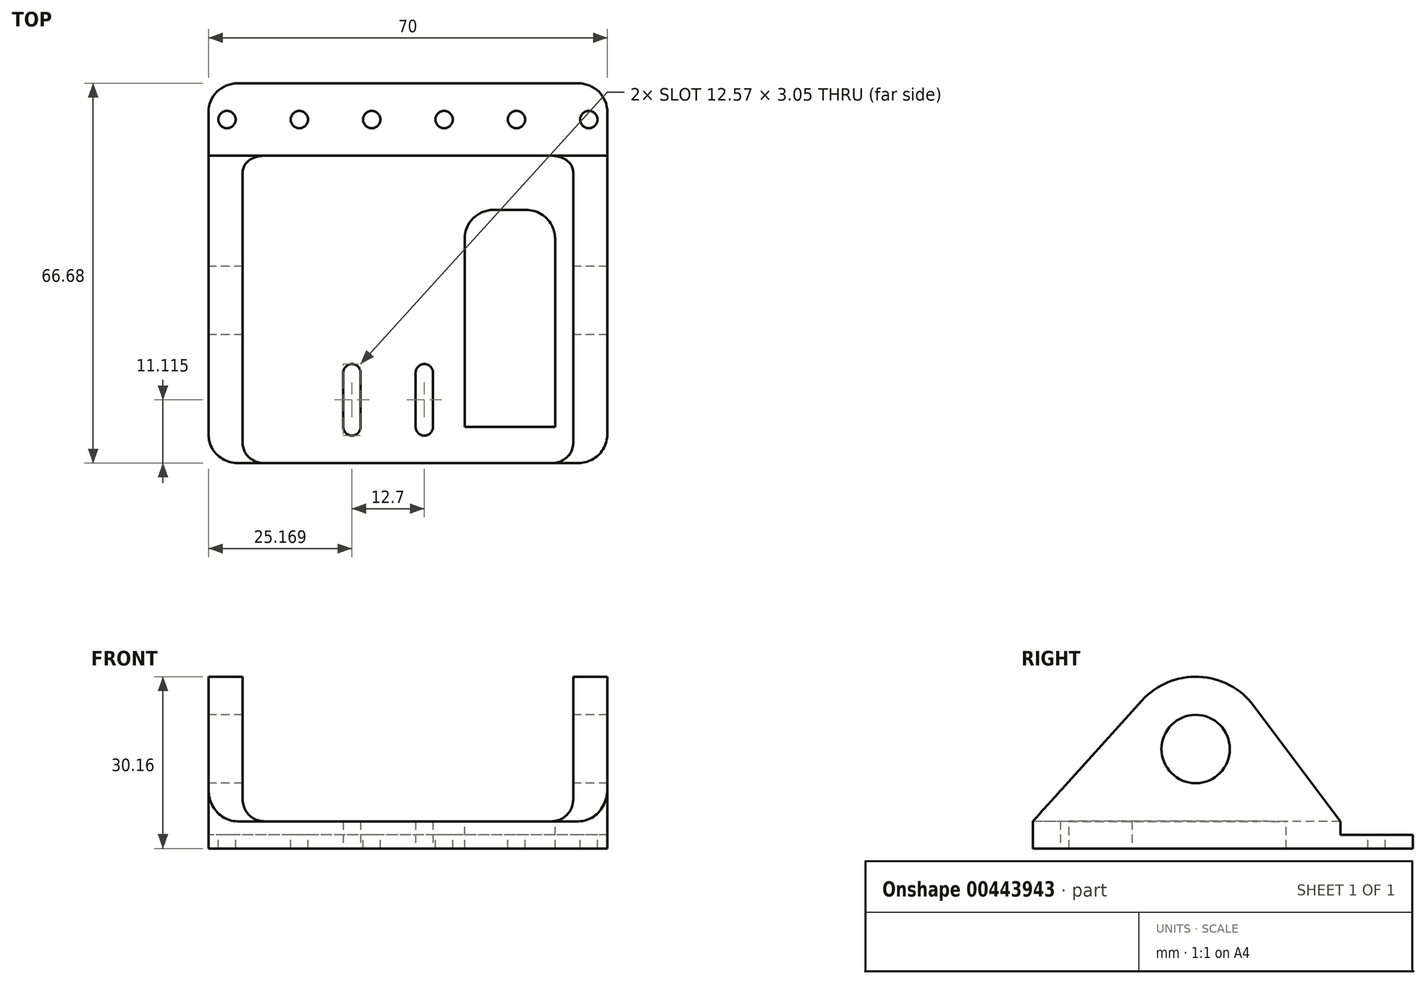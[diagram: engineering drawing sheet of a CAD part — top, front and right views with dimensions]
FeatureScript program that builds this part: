
annotation { "Feature Type Name" : "Feature", "Feature Type Description" : "" }
export const myFeature = defineFeature(function(context is Context, id is Id, definition is map)
    precondition{}
    {
        {
            var Q0;
            Q0=qCreatedBy(makeId("Top.planeOp"),FACE);
            var sketch = newSketch(context, id + "F0", { "sketchPlane" : qUnion([Q0])});
            skLineSegment(sketch, "E0.bottom", {"start": v(35, 33.34) * mm, "end": v(-35, 33.34) * mm});
            skLineSegment(sketch, "E0.top", {"start": v(35, -33.34) * mm, "end": v(-35, -33.34) * mm});
            skLineSegment(sketch, "E0.left", {"start": v(35, 33.34) * mm, "end": v(35, -33.34) * mm});
            skLineSegment(sketch, "E0.right", {"start": v(-35, 33.34) * mm, "end": v(-35, -33.34) * mm});
            skPoint(sketch, "E0.middle", {"position": v(0, 0) * mm});
            skSolve(sketch);
        }
        {
            var Q0;
            Q0=qSketchRegion(id+"F0",true);
            extrude(context, id + "F1", {"entities" : qUnion([Q0]), "depth" : 4.76 * mm});
        }
        {
            var Q0;
            Q0=makeQuery(id+"F1.opExtrude","SWEPT_FACE",FACE,{"disambiguationData":[OSD([sQuery(id+"F0.wireOp",EDGE,"E0.right")])]});
            var sketch = newSketch(context, id + "F2", { "sketchPlane" : qUnion([Q0])});
            skCircle(sketch, "E1", {"center": v(4.76, 17.46) * mm, "radius": 2 * mm});
            skCircle(sketch, "E2", {"center": v(4.76, 17.46) * mm, "radius": 6 * mm});
            skLineSegment(sketch, "E3", {"start": v(-7.94, 17.46) * mm, "end": v(-7.94, 4.76) * mm});
            skLineSegment(sketch, "E4", {"start": v(-7.94, 4.76) * mm, "end": v(17.46, 4.76) * mm});
            skLineSegment(sketch, "E5", {"start": v(17.46, 4.76) * mm, "end": v(17.46, 17.46) * mm});
            skArc(sketch, "E6", {"start": v(-7.94, 17.46) * mm, "mid": v(-4.22, 8.48) * mm, "end": v(4.76, 4.76) * mm, "construction": true});
            skArc(sketch, "E7", {"start": v(4.76, 4.76) * mm, "mid": v(13.74, 8.48) * mm, "end": v(17.46, 17.46) * mm, "construction": true});
            skArc(sketch, "E8", {"start": v(17.46, 17.46) * mm, "mid": v(4.76, 30.16) * mm, "end": v(-7.94, 17.46) * mm});
            skLineSegment(sketch, "E9", {"start": v(14.19, 25.97) * mm, "end": v(33.34, 4.76) * mm});
            skLineSegment(sketch, "E10", {"start": v(33.34, 4.76) * mm, "end": v(17.46, 4.76) * mm});
            skLineSegment(sketch, "E11", {"start": v(-5.4, 25.08) * mm, "end": v(-20.64, 4.76) * mm});
            skLineSegment(sketch, "E12", {"start": v(-20.64, 4.76) * mm, "end": v(-7.94, 4.76) * mm});
            skSolve(sketch);
        }
        {
            var Q0;
            Q0=qSketchRegion(id+"F2",true);
            var Q1;
            Q1=makeQuery(id+"F1.opExtrude","SWEPT_FACE",FACE,{"disambiguationData":[OSD([sQuery(id+"F0.wireOp",EDGE,"E0.left")])]});
            extrude(context, id + "F3", {"entities" : qUnion([Q0]), "operationType" : NewBodyOperationType.ADD, "endBound" : BoundingType.UP_TO_SURFACE, "oppositeDirection" : true, "endBoundEntityFace" : qUnion([Q1]), "depth" : 25.4 * mm});
        }
        {
            var Q0;
            Q0=makeQuery(id+"F1.opExtrude","CAP_FACE",FACE,{"disambiguationData":[OSD([sQuery(id+"F0.wireOp",EDGE,"E0.bottom"),sQuery(id+"F0.wireOp",EDGE,"E0.top"),sQuery(id+"F0.wireOp",EDGE,"E0.left"),sQuery(id+"F0.wireOp",EDGE,"E0.right")])],"isStart":false});
            var sketch = newSketch(context, id + "F4", { "sketchPlane" : qUnion([Q0])});
            skLineSegment(sketch, "E13.bottom", {"start": v(-29, 20.64) * mm, "end": v(29, 20.64) * mm});
            skLineSegment(sketch, "E13.top", {"start": v(-29, -33.34) * mm, "end": v(29, -33.34) * mm});
            skLineSegment(sketch, "E13.left", {"start": v(-29, 20.64) * mm, "end": v(-29, -33.34) * mm});
            skLineSegment(sketch, "E13.right", {"start": v(29, 20.64) * mm, "end": v(29, -33.34) * mm});
            skSolve(sketch);
        }
        {
            var Q0;
            Q0=qSketchRegion(id+"F4",true);
            extrude(context, id + "F5", {"entities" : qUnion([Q0]), "operationType" : NewBodyOperationType.REMOVE, "endBound" : BoundingType.THROUGH_ALL, "depth" : 25.4 * mm});
        }
        {
            var Q0;
            Q0=makeQuery(id+"F5.boolean.opBoolean","MERGE",FACE,{"derivedFrom":[makeQuery(id+"F1.opExtrude","CAP_FACE",FACE,{"disambiguationData":[OSD([sQuery(id+"F0.wireOp",EDGE,"E0.bottom"),sQuery(id+"F0.wireOp",EDGE,"E0.top"),sQuery(id+"F0.wireOp",EDGE,"E0.left"),sQuery(id+"F0.wireOp",EDGE,"E0.right")])],"isStart":false}),makeQuery(id+"F5.opExtrude","CAP_FACE",FACE,{"disambiguationData":[OSD([sQuery(id+"F4.wireOp",EDGE,"E13.bottom"),sQuery(id+"F4.wireOp",EDGE,"E13.top"),sQuery(id+"F4.wireOp",EDGE,"E13.left"),sQuery(id+"F4.wireOp",EDGE,"E13.right")])],"isStart":true})]});
            var sketch = newSketch(context, id + "F6", { "sketchPlane" : qUnion([Q0])});
            skLineSegment(sketch, "E14.bottom", {"start": v(25.83, -26.99) * mm, "end": v(9.95, -26.99) * mm});
            skLineSegment(sketch, "E14.top", {"start": v(25.83, 11.11) * mm, "end": v(9.95, 11.11) * mm});
            skLineSegment(sketch, "E14.left", {"start": v(25.83, -26.99) * mm, "end": v(25.83, 11.11) * mm});
            skLineSegment(sketch, "E14.right", {"start": v(9.95, -26.99) * mm, "end": v(9.95, 11.11) * mm});
            skSolve(sketch);
        }
        {
            var Q0;
            Q0=qSketchRegion(id+"F6",true);
            extrude(context, id + "F7", {"entities" : qUnion([Q0]), "operationType" : NewBodyOperationType.REMOVE, "endBound" : BoundingType.UP_TO_NEXT, "oppositeDirection" : true, "depth" : 25.4 * mm});
        }
        {
            var Q0;
            Q0=makeQuery(id+"F1.opExtrude","CAP_FACE",FACE,{"disambiguationData":[OSD([sQuery(id+"F0.wireOp",EDGE,"E0.bottom"),sQuery(id+"F0.wireOp",EDGE,"E0.top"),sQuery(id+"F0.wireOp",EDGE,"E0.left"),sQuery(id+"F0.wireOp",EDGE,"E0.right")])],"isStart":true});
            var sketch = newSketch(context, id + "F8", { "sketchPlane" : qUnion([Q0])});
            skLineSegment(sketch, "E15.bottom", {"start": v(-15.8, 33.34) * mm, "end": v(8.84, 33.34) * mm, "construction": true});
            skLineSegment(sketch, "E15.top", {"start": v(-15.8, 4.35) * mm, "end": v(8.84, 4.35) * mm, "construction": true});
            skLineSegment(sketch, "E15.left", {"start": v(-15.8, 33.34) * mm, "end": v(-15.8, 4.35) * mm, "construction": true});
            skLineSegment(sketch, "E15.right", {"start": v(8.84, 33.34) * mm, "end": v(8.84, 4.35) * mm, "construction": true});
            skLineSegment(sketch, "E16", {"start": v(-15.8, 22.23) * mm, "end": v(-9.83, 22.23) * mm, "construction": true});
            skLineSegment(sketch, "E17", {"start": v(2.87, 22.23) * mm, "end": v(8.84, 22.23) * mm, "construction": true});
            skLineSegment(sketch, "E18", {"start": v(-9.83, 22.23) * mm, "end": v(2.87, 22.23) * mm, "construction": true});
            skLineSegment(sketch, "E19.bottom", {"start": v(-11.35, 17.46) * mm, "end": v(-8.3, 17.46) * mm, "construction": true});
            skLineSegment(sketch, "E19.top", {"start": v(-11.35, 26.99) * mm, "end": v(-8.3, 26.99) * mm, "construction": true});
            skLineSegment(sketch, "E19.left", {"start": v(-11.35, 17.46) * mm, "end": v(-11.35, 26.99) * mm});
            skLineSegment(sketch, "E19.right", {"start": v(-8.3, 17.46) * mm, "end": v(-8.3, 26.99) * mm});
            skPoint(sketch, "E19.middle", {"position": v(-9.83, 22.23) * mm});
            skLineSegment(sketch, "E20.bottom", {"start": v(1.34, 17.46) * mm, "end": v(4.4, 17.46) * mm, "construction": true});
            skLineSegment(sketch, "E20.top", {"start": v(1.35, 26.99) * mm, "end": v(4.4, 26.99) * mm, "construction": true});
            skLineSegment(sketch, "E20.left", {"start": v(1.35, 17.46) * mm, "end": v(1.35, 26.99) * mm});
            skLineSegment(sketch, "E20.right", {"start": v(4.4, 17.46) * mm, "end": v(4.4, 26.99) * mm});
            skPoint(sketch, "E20.middle", {"position": v(2.87, 22.23) * mm});
            skArc(sketch, "E21", {"start": v(-11.35, 17.46) * mm, "mid": v(-9.83, 15.94) * mm, "end": v(-8.3, 17.46) * mm});
            skArc(sketch, "E22", {"start": v(1.34, 17.46) * mm, "mid": v(2.87, 15.94) * mm, "end": v(4.4, 17.46) * mm});
            skArc(sketch, "E23", {"start": v(-8.3, 26.99) * mm, "mid": v(-9.83, 28.51) * mm, "end": v(-11.35, 26.99) * mm});
            skArc(sketch, "E24", {"start": v(4.4, 26.99) * mm, "mid": v(2.87, 28.51) * mm, "end": v(1.35, 26.99) * mm});
            skSolve(sketch);
        }
        {
            var Q0;
            Q0=makeQuery(id+"F8.imprint","IMPRINT",FACE,{"disambiguationData":[TD([[makeQuery(id+"F8.imprint","IMPRINT",EDGE,{"derivedFrom":sQuery(id+"F8.wireOp",EDGE,"E20.left")}),-1.0]])]});
            var Q1;
            Q1=makeQuery(id+"F8.imprint","IMPRINT",FACE,{"disambiguationData":[TD([[makeQuery(id+"F8.imprint","IMPRINT",EDGE,{"derivedFrom":sQuery(id+"F8.wireOp",EDGE,"E19.left")}),-1.0]])]});
            extrude(context, id + "F9", {"entities" : qUnion([Q0, Q1]), "operationType" : NewBodyOperationType.REMOVE, "oppositeDirection" : true, "depth" : 25.4 * mm});
        }
        {
            var Q0;
            Q0=makeQuery(id+"FCm2X9aqr08QVEI_1.splitOp","SPLIT",FACE,{"derivedFrom":makeQuery(id+"FB7dtnONbZpMkYq_1.boolean.opBoolean","MERGE",FACE,{"derivedFrom":[makeQuery(id+"FMi2k5xwuVLF3PA_1.boolean.opBoolean","MERGE",FACE,{"derivedFrom":[makeQuery(id+"F5.boolean.opBoolean","MERGE",FACE,{"derivedFrom":[makeQuery(id+"F1.opExtrude","CAP_FACE",FACE,{"disambiguationData":[OSD([sQuery(id+"F0.wireOp",EDGE,"E0.bottom"),sQuery(id+"F0.wireOp",EDGE,"E0.top"),sQuery(id+"F0.wireOp",EDGE,"E0.left"),sQuery(id+"F0.wireOp",EDGE,"E0.right")])],"isStart":false}),makeQuery(id+"F5.opExtrude","CAP_FACE",FACE,{"disambiguationData":[OSD([sQuery(id+"F4.wireOp",EDGE,"E13.bottom"),sQuery(id+"F4.wireOp",EDGE,"E13.top"),sQuery(id+"F4.wireOp",EDGE,"E13.left"),sQuery(id+"F4.wireOp",EDGE,"E13.right")])],"isStart":true})]}),makeQuery(id+"FMi2k5xwuVLF3PA_1.opExtrude","CAP_FACE",FACE,{"disambiguationData":[OSD([sQuery(id+"FTfkWxI29d7fm9c_1.wireOp",EDGE,"U5VrA20J-yWmg-0HZa-dIx8-nOMwWomhaKgW.bottom"),sQuery(id+"FTfkWxI29d7fm9c_1.wireOp",EDGE,"U5VrA20J-yWmg-0HZa-dIx8-nOMwWomhaKgW.top"),sQuery(id+"FTfkWxI29d7fm9c_1.wireOp",EDGE,"U5VrA20J-yWmg-0HZa-dIx8-nOMwWomhaKgW.left"),sQuery(id+"FTfkWxI29d7fm9c_1.wireOp",EDGE,"U5VrA20J-yWmg-0HZa-dIx8-nOMwWomhaKgW.right")])],"isStart":false})]}),makeQuery(id+"FB7dtnONbZpMkYq_1.opExtrude","CAP_FACE",FACE,{"disambiguationData":[OSD([sQuery(id+"FrBCCQyiW6SgCSX_1.wireOp",EDGE,"mjBH3HNc-4qiW-W3lP-ZLe8-cYrq6YZMYFNo"),sQuery(id+"FrBCCQyiW6SgCSX_1.wireOp",EDGE,"n0JCGPxu-1fb2-x5wm-e2xR-ESQF5aKrQkje"),sQuery(id+"FrBCCQyiW6SgCSX_1.wireOp",EDGE,"84PFO3UT-d6lO-mKTi-YjnM-evNH14zkO4eM"),sQuery(id+"FrBCCQyiW6SgCSX_1.wireOp",EDGE,"4GRO5FYG-KxOb-3d1O-tR9n-mdH5JcoPf6cH"),sQuery(id+"FrBCCQyiW6SgCSX_1.wireOp",EDGE,"m2es6RPa-RLP1-cTb9-RGGa-vc4GqjSnDQWD"),sQuery(id+"FrBCCQyiW6SgCSX_1.wireOp",EDGE,"UMJGmRyr-7NXd-P1yE-yibc-kyMIe0C5EN52"),sQuery(id+"FrBCCQyiW6SgCSX_1.wireOp",EDGE,"6lN2ZSX2-TrvR-bXuT-GwBE-q0yeGYqzIHT5")])],"isStart":false})]}),"isFromBackBody":true});
            var sketch = newSketch(context, id + "F10", { "sketchPlane" : qUnion([Q0])});
            skLineSegment(sketch, "E25.bottom", {"start": v(-35, 33.34) * mm, "end": v(35, 33.34) * mm});
            skLineSegment(sketch, "E25.top", {"start": v(-35, 20.64) * mm, "end": v(35, 20.64) * mm});
            skLineSegment(sketch, "E26", {"start": v(35, 20.64) * mm, "end": v(35, 33.34) * mm});
            skLineSegment(sketch, "E27", {"start": v(-35, 20.64) * mm, "end": v(-35, 33.34) * mm});
            skSolve(sketch);
        }
        {
            var Q0;
            Q0=qSketchRegion(id+"F10",true);
            extrude(context, id + "F11", {"entities" : qUnion([Q0]), "operationType" : NewBodyOperationType.REMOVE, "oppositeDirection" : true, "depth" : 2.38 * mm});
        }
        {
            var Q0;
            Q0=makeQuery(id+"F11.boolean.opBoolean","COPY",FACE,{"derivedFrom":makeQuery(id+"F11.opExtrude","CAP_FACE",FACE,{"disambiguationData":[OSD([sQuery(id+"F10.wireOp",EDGE,"E25.bottom"),sQuery(id+"F10.wireOp",EDGE,"E25.top"),sQuery(id+"F10.wireOp",EDGE,"E25.left"),sQuery(id+"F10.wireOp",EDGE,"E25.right")])],"isStart":false})});
            var sketch = newSketch(context, id + "F12", { "sketchPlane" : qUnion([Q0])});
            skLineSegment(sketch, "E28", {"start": v(-19.05, 26.99) * mm, "end": v(-6.35, 26.99) * mm, "construction": true});
            skLineSegment(sketch, "E29", {"start": v(-6.35, 26.99) * mm, "end": v(6.35, 26.99) * mm, "construction": true});
            skLineSegment(sketch, "E30", {"start": v(6.35, 26.99) * mm, "end": v(19.05, 26.99) * mm, "construction": true});
            skLineSegment(sketch, "E31", {"start": v(-19.05, 26.99) * mm, "end": v(-31.75, 26.99) * mm, "construction": true});
            skLineSegment(sketch, "E32", {"start": v(19.05, 26.99) * mm, "end": v(31.75, 26.99) * mm, "construction": true});
            skLineSegment(sketch, "E33", {"start": v(31.75, 26.99) * mm, "end": v(35, 26.99) * mm, "construction": true});
            skLineSegment(sketch, "E34", {"start": v(-31.75, 26.99) * mm, "end": v(-35, 26.99) * mm, "construction": true});
            skCircle(sketch, "E35", {"center": v(-31.75, 26.99) * mm, "radius": 1.52 * mm});
            skCircle(sketch, "E36", {"center": v(-19.05, 26.99) * mm, "radius": 1.52 * mm});
            skCircle(sketch, "E37", {"center": v(-6.35, 26.99) * mm, "radius": 1.52 * mm});
            skCircle(sketch, "E38", {"center": v(6.35, 26.99) * mm, "radius": 1.52 * mm});
            skCircle(sketch, "E39", {"center": v(19.05, 26.99) * mm, "radius": 1.52 * mm});
            skCircle(sketch, "E40", {"center": v(31.75, 26.99) * mm, "radius": 1.52 * mm});
            skSolve(sketch);
        }
        {
            var Q0;
            Q0=qSketchRegion(id+"F12",true);
            extrude(context, id + "F13", {"entities" : qUnion([Q0]), "operationType" : NewBodyOperationType.REMOVE, "endBound" : BoundingType.UP_TO_NEXT, "oppositeDirection" : true, "depth" : 25.4 * mm});
        }
        {
            var Q0;
            Q0=makeQuery(id+"F1.opExtrude","SWEPT_EDGE",EDGE,{"disambiguationData":[OSD([sQuery(id+"F0.wireOp",EDGE,"E0.bottom"),sQuery(id+"F0.wireOp",EDGE,"E0.right")])]});
            var Q1;
            Q1=makeQuery(id+"F1.opExtrude","SWEPT_EDGE",EDGE,{"disambiguationData":[OSD([sQuery(id+"F0.wireOp",EDGE,"E0.bottom"),sQuery(id+"F0.wireOp",EDGE,"E0.left")])]});
            fillet(context, id + "F14", {"entities" : qUnion([Q0, Q1]), "radius" : 5.08 * mm, "tangentPropagation" : true, "allowEdgeOverflow" : false});
        }
        {
            var Q0;
            Q0=makeQuery(id+"F5.boolean.opBoolean","COPY",EDGE,{"derivedFrom":makeQuery(id+"F5.opExtrude","CAP_EDGE",EDGE,{"disambiguationData":[OSD([sQuery(id+"F4.wireOp",EDGE,"E13.left")])],"isStart":true})});
            var Q1;
            Q1=makeQuery(id+"F5.boolean.opBoolean","COPY",EDGE,{"derivedFrom":makeQuery(id+"F5.opExtrude","CAP_EDGE",EDGE,{"disambiguationData":[OSD([sQuery(id+"F4.wireOp",EDGE,"E13.right")])],"isStart":true})});
            fillet(context, id + "F15", {"entities" : qUnion([Q0, Q1]), "radius" : 3.8 * mm, "tangentPropagation" : true, "allowEdgeOverflow" : false});
        }
        {
            var Q0;
            Q0=makeQuery(id+"F1.opExtrude","SWEPT_EDGE",EDGE,{"disambiguationData":[OSD([sQuery(id+"F0.wireOp",EDGE,"E0.top"),sQuery(id+"F0.wireOp",EDGE,"E0.left")])]});
            var Q1;
            Q1=makeQuery(id+"F1.opExtrude","SWEPT_EDGE",EDGE,{"disambiguationData":[OSD([sQuery(id+"F0.wireOp",EDGE,"E0.top"),sQuery(id+"F0.wireOp",EDGE,"E0.right")])]});
            fillet(context, id + "F16", {"entities" : qUnion([Q0, Q1]), "radius" : 5.08 * mm, "tangentPropagation" : true, "allowEdgeOverflow" : false});
        }
        {
            var Q0;
            {var subQ0=sQuery(id+"F6.wireOp",EDGE,"E14.left");var subQ1=sQuery(id+"F6.wireOp",EDGE,"E14.top");Q0=makeQuery(id+"F11.boolean.opBoolean","SPLIT",EDGE,{"disambiguationData":[TD([makeQuery(id+"F1.opExtrude","CAP_FACE",FACE,{"disambiguationData":[OSD([sQuery(id+"F0.wireOp",EDGE,"E0.bottom"),sQuery(id+"F0.wireOp",EDGE,"E0.top"),sQuery(id+"F0.wireOp",EDGE,"E0.left"),sQuery(id+"F0.wireOp",EDGE,"E0.right")])],"isStart":true})])],"derivedFrom":makeQuery(id+"F7.boolean.opBoolean","COPY",EDGE,{"derivedFrom":makeQuery(id+"F7.opExtrude","SWEPT_EDGE",EDGE,{"disambiguationData":[OSD([subQ1,subQ0])]})})});}
            var Q1;
            {var subQ0=sQuery(id+"F6.wireOp",EDGE,"E14.right");var subQ1=sQuery(id+"F6.wireOp",EDGE,"E14.top");Q1=makeQuery(id+"F11.boolean.opBoolean","SPLIT",EDGE,{"disambiguationData":[TD([makeQuery(id+"F1.opExtrude","CAP_FACE",FACE,{"disambiguationData":[OSD([sQuery(id+"F0.wireOp",EDGE,"E0.bottom"),sQuery(id+"F0.wireOp",EDGE,"E0.top"),sQuery(id+"F0.wireOp",EDGE,"E0.left"),sQuery(id+"F0.wireOp",EDGE,"E0.right")])],"isStart":true})])],"derivedFrom":makeQuery(id+"F7.boolean.opBoolean","COPY",EDGE,{"derivedFrom":makeQuery(id+"F7.opExtrude","SWEPT_EDGE",EDGE,{"disambiguationData":[OSD([subQ1,subQ0])]})})});}
            fillet(context, id + "F17", {"entities" : qUnion([Q0, Q1]), "radius" : 5.08 * mm, "tangentPropagation" : true, "allowEdgeOverflow" : false});
        }
    });
